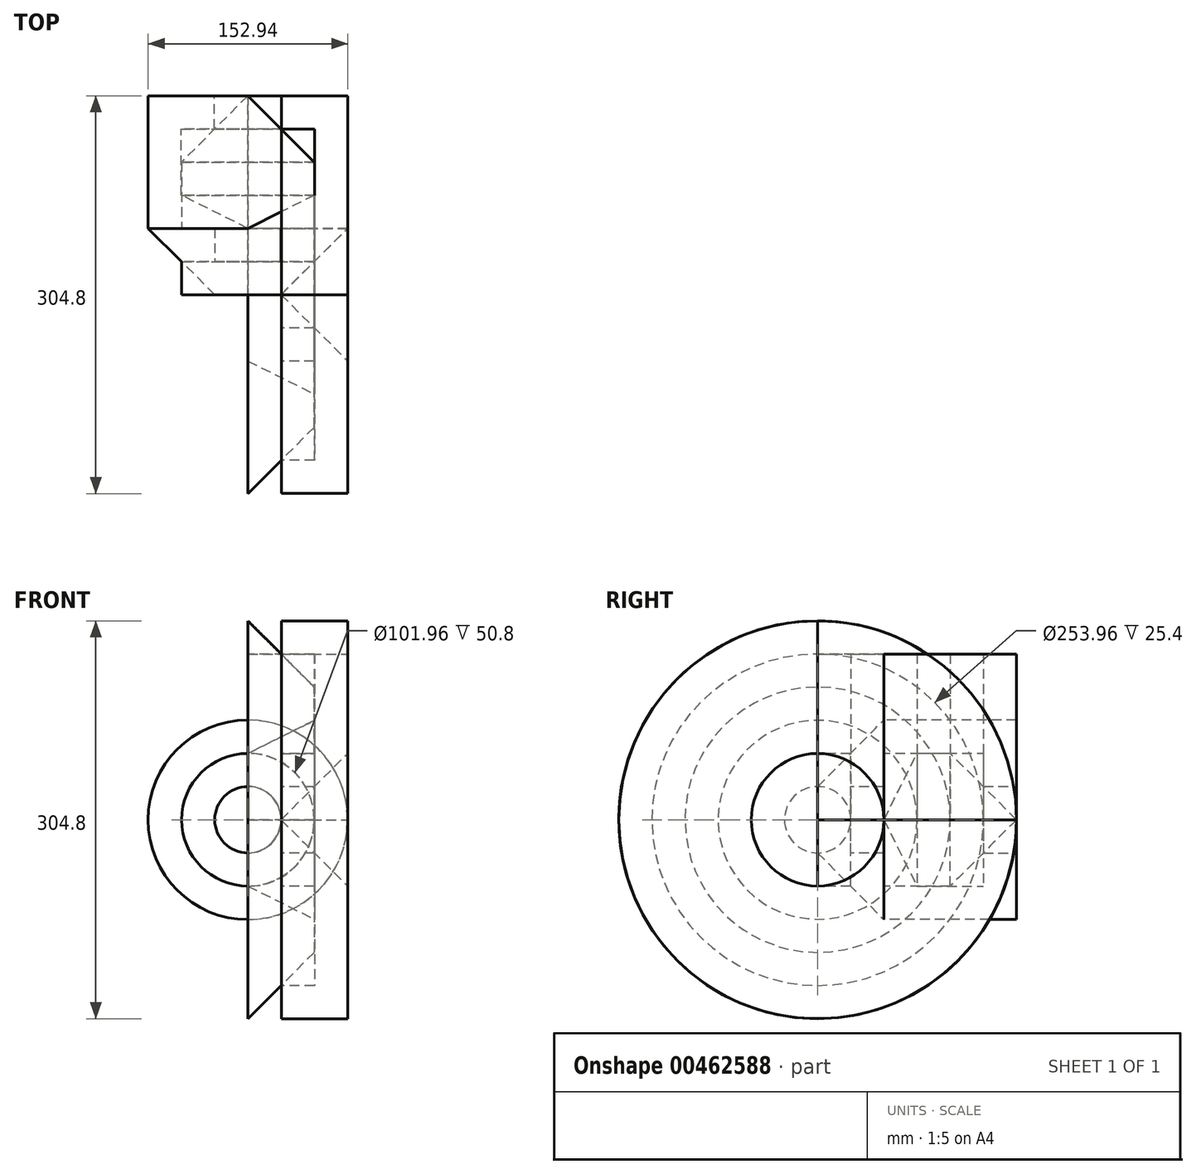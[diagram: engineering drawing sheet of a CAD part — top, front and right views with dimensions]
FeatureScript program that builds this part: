
annotation { "Feature Type Name" : "Feature", "Feature Type Description" : "" }
export const myFeature = defineFeature(function(context is Context, id is Id, definition is map)
    precondition{}
    {
        {
            var Q0;
            Q0=qCreatedBy(makeId("Top.planeOp"),FACE);
            var sketch = newSketch(context, id + "F0", { "sketchPlane" : qUnion([Q0])});
            skLineSegment(sketch, "E0", {"start": v(0, 0) * mm, "end": v(50.8, 0) * mm});
            skLineSegment(sketch, "E1", {"start": v(50.8, 0) * mm, "end": v(50.8, 25.4) * mm});
            skLineSegment(sketch, "E2", {"start": v(50.8, 25.4) * mm, "end": v(25.4, 25.4) * mm});
            skLineSegment(sketch, "E3", {"start": v(25.4, 25.4) * mm, "end": v(25.4, 50.8) * mm});
            skLineSegment(sketch, "E4", {"start": v(25.4, 50.8) * mm, "end": v(50.8, 50.8) * mm});
            skLineSegment(sketch, "E5", {"start": v(50.8, 50.8) * mm, "end": v(50.8, 101.6) * mm});
            skLineSegment(sketch, "E6", {"start": v(0, 0) * mm, "end": v(0, 152.4) * mm});
            skLineSegment(sketch, "E7", {"start": v(0, 152.4) * mm, "end": v(50.8, 101.6) * mm});
            skSolve(sketch);
        }
        {
            var Q0;
            Q0 = qSketchRegion(id + "F0", true);
            extrude(context, id + "F1", {"entities" : qUnion([Q0]), "depth" : 127 * mm});
        }
        {
            var Q0;
            Q0=makeQuery(id+"F0.imprint","IMPRINT",FACE,{"disambiguationData":[TD([[makeQuery(id+"F0.imprint","IMPRINT",EDGE,{"derivedFrom":sQuery(id+"F0.wireOp",EDGE,"E0")}),1.0]])]});
            var Q1;
            Q1=sQuery(id+"F0.wireOp",EDGE,"E0");
            revolve(context, id + "F2", {"entities" : qUnion([Q0]), "axis" : qUnion([Q1]), "revolveType" : RevolveType.FULL});
        }
        {
            var Q0;
            Q0=makeQuery(id+"F0.imprint","IMPRINT",FACE,{"disambiguationData":[TD([[makeQuery(id+"F0.imprint","IMPRINT",EDGE,{"derivedFrom":sQuery(id+"F0.wireOp",EDGE,"E0")}),1.0]])]});
            var Q1;
            Q1=sQuery(id+"F0.wireOp",EDGE,"E6");
            revolve(context, id + "F3", {"entities" : qUnion([Q0]), "axis" : qUnion([Q1]), "revolveType" : RevolveType.FULL});
        }
        {
            var Q0;
            Q0=makeQuery(id+"F0.imprint","IMPRINT",FACE,{"disambiguationData":[TD([[makeQuery(id+"F0.imprint","IMPRINT",EDGE,{"derivedFrom":sQuery(id+"F0.wireOp",EDGE,"E0")}),1.0]])]});
            var Q1;
            Q1=sQuery(id+"F0.wireOp",EDGE,"E0");
            revolve(context, id + "F4", {"entities" : qUnion([Q0]), "axis" : qUnion([Q1]), "revolveType" : RevolveType.ONE_DIRECTION, "angle" : 90 * degree});
        }
        {
            var Q0;
            Q0=qCreatedBy(makeId("Top.planeOp"),FACE);
            var sketch = newSketch(context, id + "F5", { "sketchPlane" : qUnion([Q0])});
            skLineSegment(sketch, "E8", {"start": v(0, 50.8) * mm, "end": v(0, 0) * mm});
            skLineSegment(sketch, "E9", {"start": v(0, 0) * mm, "end": v(25.4, 0) * mm});
            skLineSegment(sketch, "E10", {"start": v(25.4, 0) * mm, "end": v(76.47, 50.78) * mm});
            skLineSegment(sketch, "E11", {"start": v(25.58, 152.38) * mm, "end": v(25.58, 126.98) * mm});
            skLineSegment(sketch, "E12", {"start": v(25.58, 152.38) * mm, "end": v(76.38, 152.38) * mm});
            skLineSegment(sketch, "E13", {"start": v(76.47, 50.78) * mm, "end": v(76.38, 152.38) * mm});
            skLineSegment(sketch, "E14", {"start": v(25.58, 126.98) * mm, "end": v(50.98, 126.98) * mm});
            skLineSegment(sketch, "E15", {"start": v(50.98, 126.98) * mm, "end": v(50.98, 76.18) * mm});
            skLineSegment(sketch, "E16", {"start": v(50.98, 76.18) * mm, "end": v(0, 50.8) * mm});
            skSolve(sketch);
        }
        {
            var Q0;
            Q0=makeQuery(id+"F5.imprint","IMPRINT",FACE,{"disambiguationData":[TD([[makeQuery(id+"F5.imprint","IMPRINT",EDGE,{"derivedFrom":sQuery(id+"F5.wireOp",EDGE,"E8")}),1.0]])]});
            extrude(context, id + "F6", {"entities" : qUnion([Q0]), "depth" : 127 * mm});
        }
        {
            var Q0;
            Q0=makeQuery(id+"F5.imprint","IMPRINT",FACE,{"disambiguationData":[TD([[makeQuery(id+"F5.imprint","IMPRINT",EDGE,{"derivedFrom":sQuery(id+"F5.wireOp",EDGE,"E8")}),1.0]])]});
            var Q1;
            Q1=sQuery(id+"F5.wireOp",EDGE,"E8");
            revolve(context, id + "F7", {"entities" : qUnion([Q0]), "axis" : qUnion([Q1]), "revolveType" : RevolveType.FULL});
        }
        {
            var Q0;
            Q0=makeQuery(id+"F5.imprint","IMPRINT",FACE,{"disambiguationData":[TD([[makeQuery(id+"F5.imprint","IMPRINT",EDGE,{"derivedFrom":sQuery(id+"F5.wireOp",EDGE,"E8")}),1.0]])]});
            var Q1;
            Q1=sQuery(id+"F5.wireOp",EDGE,"E9");
            revolve(context, id + "F8", {"entities" : qUnion([Q0]), "axis" : qUnion([Q1]), "revolveType" : RevolveType.FULL});
        }
        {
            var Q0;
            Q0=makeQuery(id+"F5.imprint","IMPRINT",FACE,{"disambiguationData":[TD([[makeQuery(id+"F5.imprint","IMPRINT",EDGE,{"derivedFrom":sQuery(id+"F5.wireOp",EDGE,"E8")}),1.0]])]});
            var Q1;
            Q1=sQuery(id+"F5.wireOp",EDGE,"E9");
            revolve(context, id + "F9", {"entities" : qUnion([Q0]), "axis" : qUnion([Q1]), "revolveType" : RevolveType.ONE_DIRECTION, "angle" : 90 * degree});
        }
    });
